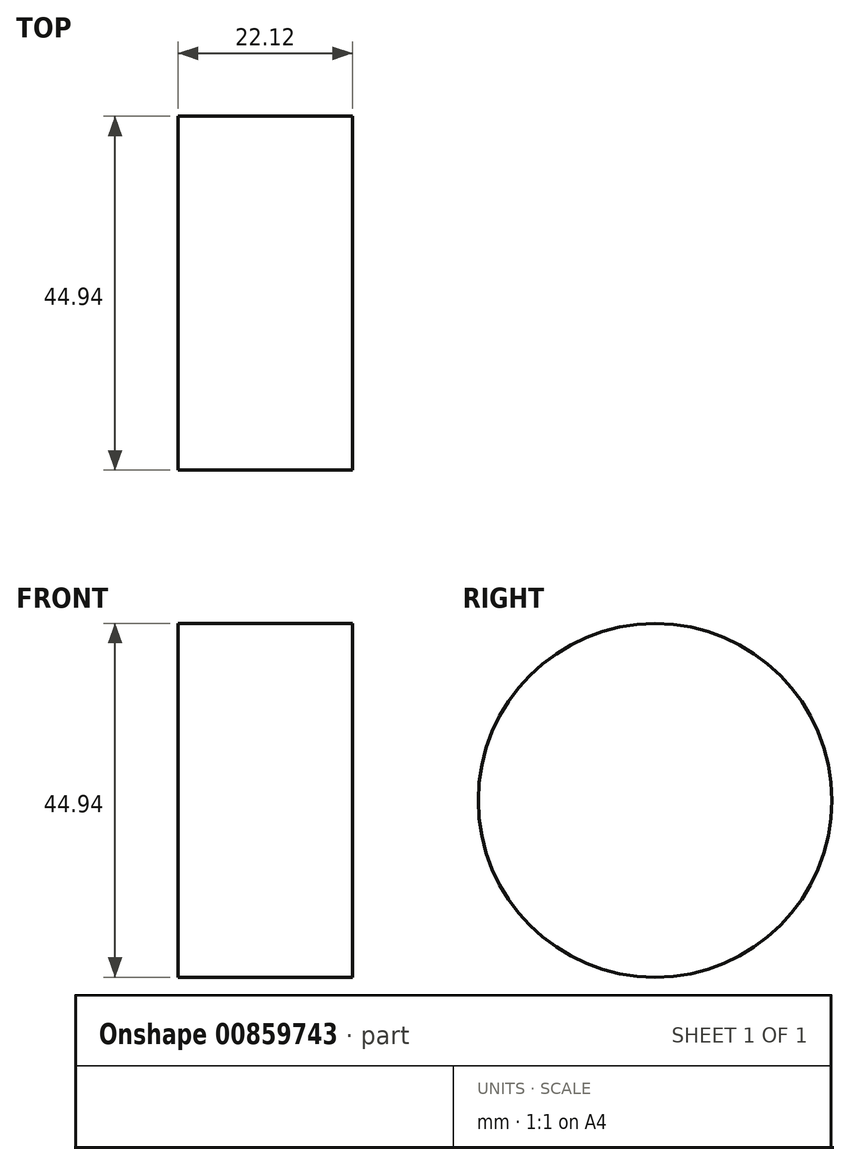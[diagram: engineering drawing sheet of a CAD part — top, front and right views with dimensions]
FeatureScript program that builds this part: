
annotation { "Feature Type Name" : "Feature", "Feature Type Description" : "" }
export const myFeature = defineFeature(function(context is Context, id is Id, definition is map)
    precondition{}
    {
        {
            var Q0;
            Q0=qCreatedBy(makeId("Right.planeOp"),FACE);
            var sketch = newSketch(context, id + "F0", { "sketchPlane" : qUnion([Q0])});
            skCircle(sketch, "E0", {"center": v(0, 0) * mm, "radius": 22.47 * mm});
            skSolve(sketch);
        }
        {
            var Q0;
            Q0=makeQuery(id+"F0.imprint","IMPRINT",FACE,{"disambiguationData":[TD([[makeQuery(id+"F0.imprint","IMPRINT",EDGE,{"derivedFrom":sQuery(id+"F0.wireOp",EDGE,"E0")}),1.0]])]});
            extrude(context, id + "F1", {"entities" : qUnion([Q0]), "endBound" : BoundingType.SYMMETRIC, "depth" : 22.13 * mm, "offsetDistance" : 25 * mm});
        }
    });
